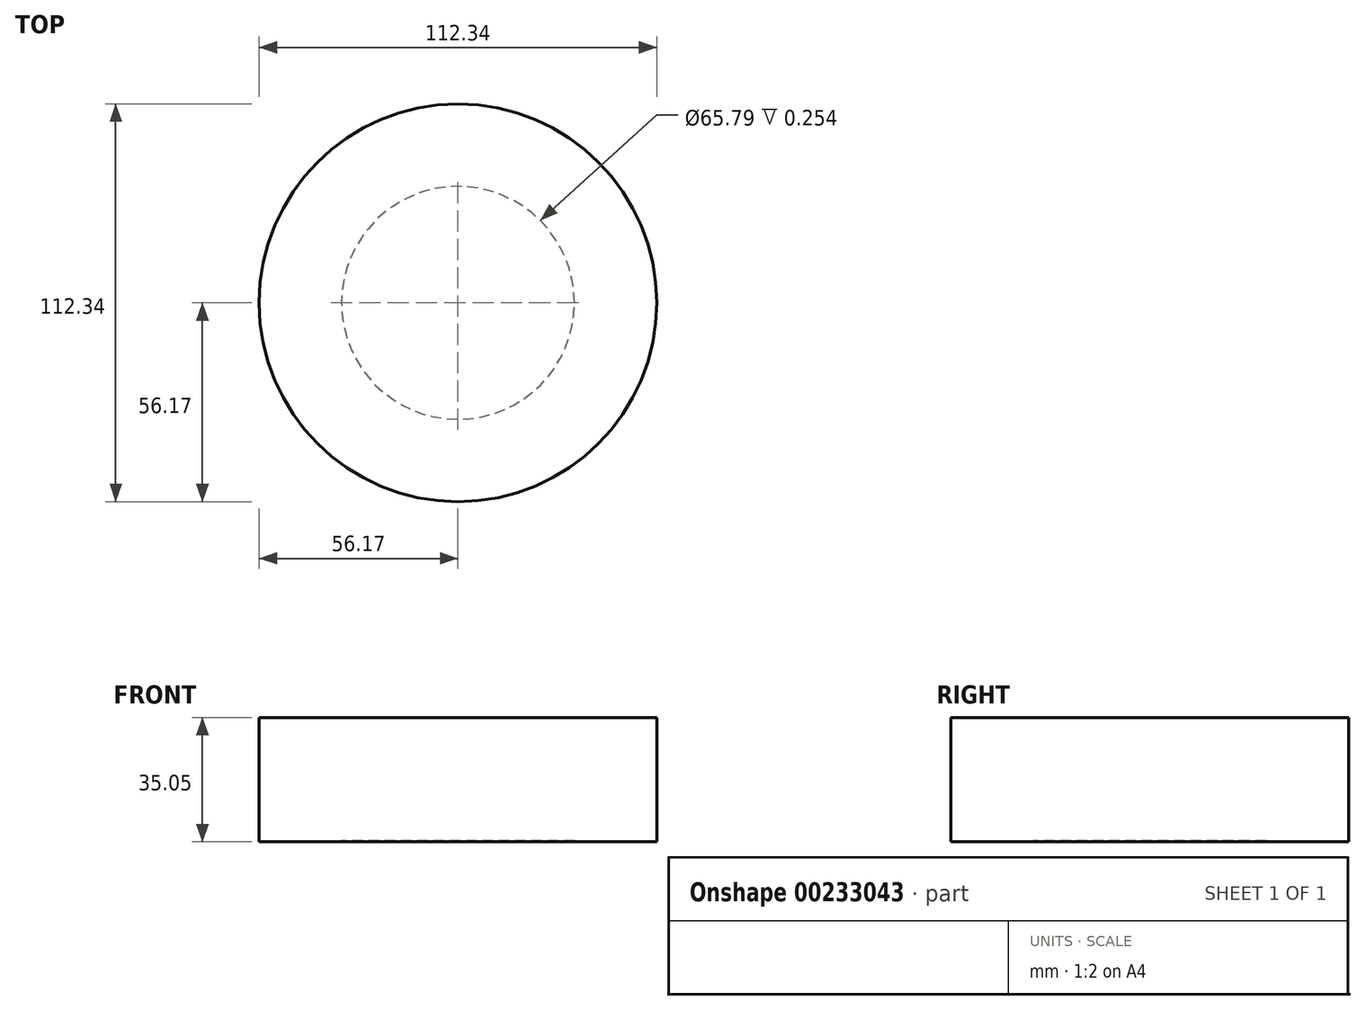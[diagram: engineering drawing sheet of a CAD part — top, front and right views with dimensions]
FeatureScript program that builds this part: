
annotation { "Feature Type Name" : "Feature", "Feature Type Description" : "" }
export const myFeature = defineFeature(function(context is Context, id is Id, definition is map)
    precondition{}
    {
        {
            var Q0;
            Q0=qCreatedBy(makeId("Top.planeOp"),FACE);
            var sketch = newSketch(context, id + "F0", { "sketchPlane" : qUnion([Q0])});
            skCircle(sketch, "E0", {"center": v(0, 0) * mm, "radius": 56.17 * mm});
            skCircle(sketch, "E1", {"center": v(0, 0) * mm, "radius": 32.9 * mm});
            skCircle(sketch, "E2", {"center": v(0, 0) * mm, "radius": 4.95 * mm});
            skCircle(sketch, "E3.cCircle", {"center": v(0, 0) * mm, "radius": 9.34 * mm, "construction": true});
            skLineSegment(sketch, "E3.0", {"start": v(8.82, -6.2) * mm, "end": v(-0.97, -10.74) * mm});
            skLineSegment(sketch, "E3.1", {"start": v(-0.97, -10.74) * mm, "end": v(-9.79, -4.54) * mm});
            skLineSegment(sketch, "E3.2", {"start": v(-9.79, -4.54) * mm, "end": v(-8.82, 6.2) * mm});
            skLineSegment(sketch, "E3.3", {"start": v(-8.82, 6.2) * mm, "end": v(0.97, 10.74) * mm});
            skLineSegment(sketch, "E3.4", {"start": v(0.97, 10.74) * mm, "end": v(9.79, 4.54) * mm});
            skLineSegment(sketch, "E3.5", {"start": v(9.79, 4.54) * mm, "end": v(8.82, -6.2) * mm});
            skPoint(sketch, "E3.0.midPoint", {"position": v(3.93, -8.48) * mm});
            skCircle(sketch, "E4.cCircle", {"center": v(0, 0) * mm, "radius": 13.2 * mm, "construction": true});
            skLineSegment(sketch, "E4.0", {"start": v(7.63, -13.2) * mm, "end": v(-7.63, -13.2) * mm});
            skLineSegment(sketch, "E4.1", {"start": v(-7.63, -13.2) * mm, "end": v(-15.25, 0) * mm});
            skLineSegment(sketch, "E4.2", {"start": v(-15.25, 0) * mm, "end": v(-7.63, 13.2) * mm});
            skLineSegment(sketch, "E4.3", {"start": v(-7.63, 13.2) * mm, "end": v(7.63, 13.2) * mm});
            skLineSegment(sketch, "E4.4", {"start": v(7.63, 13.2) * mm, "end": v(15.25, 0) * mm});
            skLineSegment(sketch, "E4.5", {"start": v(15.25, 0) * mm, "end": v(7.63, -13.2) * mm});
            skPoint(sketch, "E4.0.midPoint", {"position": v(0, -13.2) * mm});
            skCircle(sketch, "E5.cCircle", {"center": v(0, 0) * mm, "radius": 17.18 * mm, "construction": true});
            skLineSegment(sketch, "E5.0", {"start": v(17.83, -8.7) * mm, "end": v(1.39, -19.79) * mm});
            skLineSegment(sketch, "E5.1", {"start": v(1.39, -19.79) * mm, "end": v(-16.44, -11.1) * mm});
            skLineSegment(sketch, "E5.2", {"start": v(-16.44, -11.1) * mm, "end": v(-17.83, 8.7) * mm});
            skLineSegment(sketch, "E5.3", {"start": v(-17.83, 8.7) * mm, "end": v(-1.39, 19.79) * mm});
            skLineSegment(sketch, "E5.4", {"start": v(-1.39, 19.79) * mm, "end": v(16.44, 11.1) * mm});
            skLineSegment(sketch, "E5.5", {"start": v(16.44, 11.1) * mm, "end": v(17.83, -8.7) * mm});
            skPoint(sketch, "E5.0.midPoint", {"position": v(9.6, -14.24) * mm});
            skCircle(sketch, "E6.cCircle", {"center": v(0, 0) * mm, "radius": 20.86 * mm, "construction": true});
            skLineSegment(sketch, "E6.0", {"start": v(12.04, -20.86) * mm, "end": v(-12.04, -20.86) * mm});
            skLineSegment(sketch, "E6.1", {"start": v(-12.04, -20.86) * mm, "end": v(-24.08, 0) * mm});
            skLineSegment(sketch, "E6.2", {"start": v(-24.08, 0) * mm, "end": v(-12.04, 20.86) * mm});
            skLineSegment(sketch, "E6.3", {"start": v(-12.04, 20.86) * mm, "end": v(12.04, 20.86) * mm});
            skLineSegment(sketch, "E6.4", {"start": v(12.04, 20.86) * mm, "end": v(24.08, 0) * mm});
            skLineSegment(sketch, "E6.5", {"start": v(24.08, 0) * mm, "end": v(12.04, -20.86) * mm});
            skPoint(sketch, "E6.0.midPoint", {"position": v(0, -20.86) * mm});
            skCircle(sketch, "E7.cCircle", {"center": v(0, 0) * mm, "radius": 24.8 * mm, "construction": true});
            skLineSegment(sketch, "E7.0", {"start": v(25.47, -13.1) * mm, "end": v(1.4, -28.61) * mm});
            skLineSegment(sketch, "E7.1", {"start": v(1.4, -28.61) * mm, "end": v(-24.08, -15.51) * mm});
            skLineSegment(sketch, "E7.2", {"start": v(-24.08, -15.51) * mm, "end": v(-25.47, 13.1) * mm});
            skLineSegment(sketch, "E7.3", {"start": v(-25.47, 13.1) * mm, "end": v(-1.4, 28.61) * mm});
            skLineSegment(sketch, "E7.4", {"start": v(-1.4, 28.61) * mm, "end": v(24.08, 15.51) * mm});
            skLineSegment(sketch, "E7.5", {"start": v(24.08, 15.51) * mm, "end": v(25.47, -13.1) * mm});
            skPoint(sketch, "E7.0.midPoint", {"position": v(13.43, -20.86) * mm});
            skSolve(sketch);
        }
        {
            var Q0;
            Q0=makeQuery(id+"F0.imprint","IMPRINT",FACE,{"disambiguationData":[TD([[makeQuery(id+"F0.imprint","IMPRINT",EDGE,{"derivedFrom":sQuery(id+"F0.wireOp",EDGE,"E0")}),1.0]])]});
            extrude(context, id + "F1", {"entities" : qUnion([Q0]), "oppositeDirection" : true, "depth" : 35.05 * mm});
        }
        {
            var Q0;
            Q0=makeQuery(id+"F0.imprint","IMPRINT",FACE,{"disambiguationData":[TD([[makeQuery(id+"F0.imprint","IMPRINT",EDGE,{"derivedFrom":sQuery(id+"F0.wireOp",EDGE,"E1")}),1.0]])]});
            extrude(context, id + "F2", {"entities" : qUnion([Q0]), "operationType" : NewBodyOperationType.ADD, "oppositeDirection" : true, "depth" : 34.8 * mm});
        }
        {
            var Q0;
            Q0=makeQuery(id+"F0.imprint","IMPRINT",FACE,{"disambiguationData":[TD([[makeQuery(id+"F0.imprint","IMPRINT",EDGE,{"derivedFrom":sQuery(id+"F0.wireOp",EDGE,"E6.0")}),1.0]])]});
            var Q1;
            Q1=makeQuery(id+"F0.imprint","IMPRINT",FACE,{"disambiguationData":[TD([[makeQuery(id+"F0.imprint","IMPRINT",EDGE,{"derivedFrom":sQuery(id+"F0.wireOp",EDGE,"E4.0")}),1.0]])]});
            var Q2;
            Q2=makeQuery(id+"F0.imprint","IMPRINT",FACE,{"disambiguationData":[TD([[makeQuery(id+"F0.imprint","IMPRINT",EDGE,{"derivedFrom":sQuery(id+"F0.wireOp",EDGE,"E5.0")}),1.0]])]});
            var Q3;
            Q3=makeQuery(id+"F0.imprint","IMPRINT",FACE,{"disambiguationData":[TD([[makeQuery(id+"F0.imprint","IMPRINT",EDGE,{"derivedFrom":sQuery(id+"F0.wireOp",EDGE,"E2")}),-1.0]])]});
            var Q4;
            Q4=makeQuery(id+"F0.imprint","IMPRINT",FACE,{"disambiguationData":[TD([[makeQuery(id+"F0.imprint","IMPRINT",EDGE,{"derivedFrom":sQuery(id+"F0.wireOp",EDGE,"E3.0")}),1.0]])]});
            var Q5;
            Q5=makeQuery(id+"F0.imprint","IMPRINT",FACE,{"disambiguationData":[TD([[makeQuery(id+"F0.imprint","IMPRINT",EDGE,{"derivedFrom":sQuery(id+"F0.wireOp",EDGE,"E2")}),1.0]])]});
            extrude(context, id + "F3", {"entities" : qUnion([Q0, Q1, Q2, Q3, Q4, Q5]), "operationType" : NewBodyOperationType.ADD, "oppositeDirection" : true, "depth" : 34.8 * mm});
        }
    });
